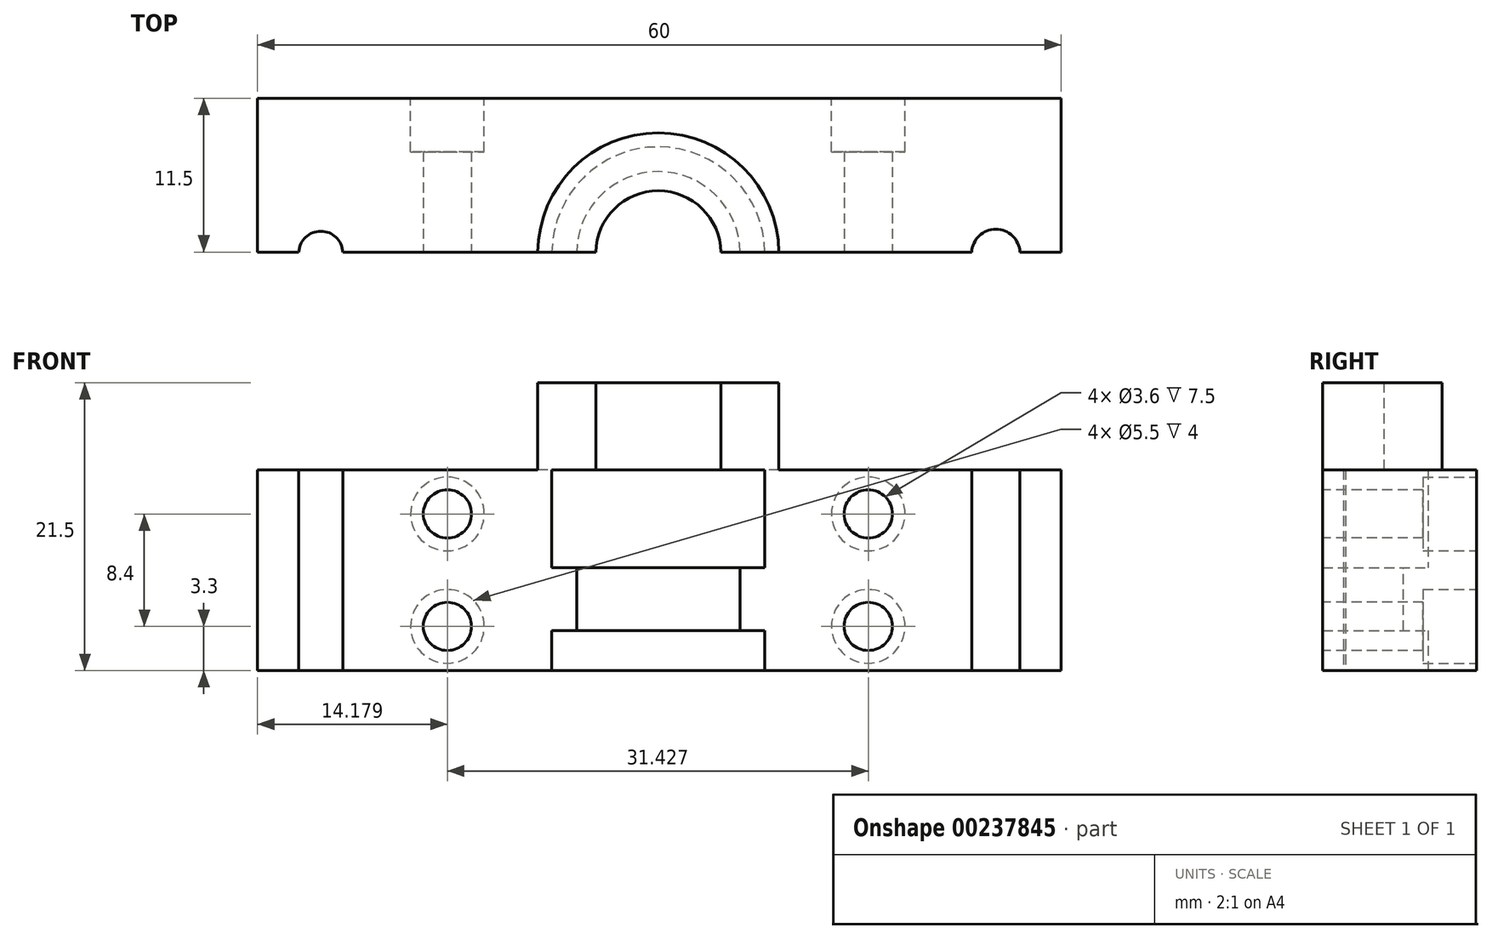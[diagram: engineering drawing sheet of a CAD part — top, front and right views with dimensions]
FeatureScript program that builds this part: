
annotation { "Feature Type Name" : "Feature", "Feature Type Description" : "" }
export const myFeature = defineFeature(function(context is Context, id is Id, definition is map)
    precondition{}
    {
        {
            var Q0;
            Q0=qCreatedBy(makeId("Top.planeOp"),FACE);
            var sketch = newSketch(context, id + "F0", { "sketchPlane" : qUnion([Q0])});
            skArc(sketch, "E0", {"start": v(7.95, 0.09) * mm, "mid": v(0, 7.95) * mm, "end": v(-7.95, 0.09) * mm});
            skArc(sketch, "E1", {"start": v(-23.55, 0.09) * mm, "mid": v(-25.2, 1.65) * mm, "end": v(-26.85, 0.09) * mm});
            skArc(sketch, "E2", {"start": v(27, 0.09) * mm, "mid": v(25.2, 1.8) * mm, "end": v(23.4, 0.09) * mm});
            skLineSegment(sketch, "E3.bottom", {"start": v(-29.93, 11.59) * mm, "end": v(30.07, 11.59) * mm});
            skLineSegment(sketch, "E3.left", {"start": v(-29.93, 11.59) * mm, "end": v(-29.93, 0.09) * mm});
            skLineSegment(sketch, "E3.right", {"start": v(30.07, 11.59) * mm, "end": v(30.07, 0.09) * mm});
            skLineSegment(sketch, "E4", {"start": v(-29.93, 0.09) * mm, "end": v(30.07, 0.09) * mm});
            skSolve(sketch);
        }
        {
            var Q0;
            Q0=makeQuery(id+"F0.imprint","IMPRINT",FACE,{"disambiguationData":[TD([[makeQuery(id+"F0.imprint","IMPRINT",EDGE,{"derivedFrom":sQuery(id+"F0.wireOp",EDGE,"E0")}),-1.0]])]});
            extrude(context, id + "F1", {"entities" : qUnion([Q0]), "depth" : 15 * mm});
        }
        {
            var Q0;
            Q0=qCreatedBy(makeId("Front.planeOp"),FACE);
            var sketch = newSketch(context, id + "F2", { "sketchPlane" : qUnion([Q0])});
            skLineSegment(sketch, "E5.bottom", {"start": v(-8, 7.7) * mm, "end": v(-6.1, 7.7) * mm});
            skLineSegment(sketch, "E5.top", {"start": v(-7.97, 3) * mm, "end": v(-6.1, 3) * mm});
            skLineSegment(sketch, "E5.right", {"start": v(-6.1, 7.7) * mm, "end": v(-6.1, 3) * mm});
            skLineSegment(sketch, "E6", {"start": v(-8, 7.7) * mm, "end": v(-7.97, 3) * mm});
            skLineSegment(sketch, "E7", {"start": v(0, 16.18) * mm, "end": v(0, -1.04) * mm, "construction": true});
            skSolve(sketch);
        }
        {
            var Q0;
            Q0 = qSketchRegion(id + "F2", true);
            var Q1;
            Q1=makeQuery(id+"F1.opExtrude","SWEPT_FACE",FACE,{"disambiguationData":[OSD([sQuery(id+"F0.wireOp",EDGE,"E0")])]});
            revolve(context, id + "F3", {"operationType" : NewBodyOperationType.ADD, "entities" : qUnion([Q0]), "axis" : qUnion([Q1]), "revolveType" : RevolveType.ONE_DIRECTION, "oppositeDirection" : true, "angle" : 180 * degree});
        }
        {
            var Q0;
            {var subQ0=sQuery(id+"F0.wireOp",EDGE,"E4");Q0=makeQuery(id+"F1.opExtrude","SWEPT_FACE",FACE,{"disambiguationData":[OSD([subQ0]),TDD([makeQuery(id+"F0.imprint","IMPRINT",EDGE,{"disambiguationData":[TD([[makeQuery(id+"F0.imprint","INTERSECT",VERTEX,{"disambiguationData":[OD(1.0)],"derivedFrom":[sQuery(id+"F0.wireOp",EDGE,"E0"),subQ0]}),1.0]])],"derivedFrom":subQ0})])]});}
            var sketch = newSketch(context, id + "F4", { "sketchPlane" : qUnion([Q0])});
            skLineSegment(sketch, "E8", {"start": v(-15.75, 15) * mm, "end": v(-15.75, 0) * mm, "construction": true});
            skPoint(sketch, "E9.endSnap0", {"position": v(-23.55, 7.5) * mm});
            skLineSegment(sketch, "E10", {"start": v(-23.55, 7.5) * mm, "end": v(-7.95, 7.5) * mm, "construction": true});
            skCircle(sketch, "E11", {"center": v(-15.75, 11.7) * mm, "radius": 1.8 * mm});
            skCircle(sketch, "E12", {"center": v(-15.75, 3.3) * mm, "radius": 1.8 * mm});
            skSolve(sketch);
        }
        {
            var Q0;
            Q0 = qSketchRegion(id + "F4", true);
            extrude(context, id + "F5", {"entities" : qUnion([Q0]), "operationType" : NewBodyOperationType.REMOVE, "oppositeDirection" : true, "depth" : 25 * mm});
        }
        {
            var Q0;
            {var subQ0=sQuery(id+"F0.wireOp",EDGE,"E4");Q0=makeQuery(id+"F1.opExtrude","SWEPT_FACE",FACE,{"disambiguationData":[OSD([subQ0]),TDD([makeQuery(id+"F0.imprint","IMPRINT",EDGE,{"disambiguationData":[TD([[makeQuery(id+"F0.imprint","INTERSECT",VERTEX,{"disambiguationData":[OD(0.0)],"derivedFrom":[sQuery(id+"F0.wireOp",EDGE,"E0"),subQ0]}),-1.0]])],"derivedFrom":subQ0})])]});}
            var sketch = newSketch(context, id + "F6", { "sketchPlane" : qUnion([Q0])});
            skLineSegment(sketch, "E13", {"start": v(15.68, 15) * mm, "end": v(15.68, 0) * mm, "construction": true});
            skLineSegment(sketch, "E14", {"start": v(23.4, 7.5) * mm, "end": v(7.95, 7.5) * mm, "construction": true});
            skCircle(sketch, "E15", {"center": v(15.68, 11.7) * mm, "radius": 1.8 * mm});
            skCircle(sketch, "E16", {"center": v(15.68, 3.3) * mm, "radius": 1.8 * mm});
            skSolve(sketch);
        }
        {
            var Q0;
            Q0 = qSketchRegion(id + "F6", true);
            extrude(context, id + "F7", {"entities" : qUnion([Q0]), "operationType" : NewBodyOperationType.REMOVE, "oppositeDirection" : true, "depth" : 25 * mm});
        }
        {
            var Q0;
            Q0=makeQuery(id+"F1.opExtrude","CAP_FACE",FACE,{"disambiguationData":[OSD([sQuery(id+"F0.wireOp",EDGE,"E0"),sQuery(id+"F0.wireOp",EDGE,"E1"),sQuery(id+"F0.wireOp",EDGE,"E2"),sQuery(id+"F0.wireOp",EDGE,"E3.bottom"),sQuery(id+"F0.wireOp",EDGE,"E3.left"),sQuery(id+"F0.wireOp",EDGE,"E3.right"),sQuery(id+"F0.wireOp",EDGE,"E4")])],"isStart":false});
            var sketch = newSketch(context, id + "F8", { "sketchPlane" : qUnion([Q0])});
            skArc(sketch, "E17", {"start": v(9, 0.09) * mm, "mid": v(0, 9) * mm, "end": v(-9, 0.09) * mm});
            skLineSegment(sketch, "E18", {"start": v(-9, 0.09) * mm, "end": v(9, 0.09) * mm});
            skSolve(sketch);
        }
        {
            var Q0;
            Q0 = qSketchRegion(id + "F8", true);
            extrude(context, id + "F9", {"entities" : qUnion([Q0]), "operationType" : NewBodyOperationType.ADD, "depth" : 6.5 * mm});
        }
        {
            var Q0;
            Q0=makeQuery(id+"F9.opExtrude","CAP_FACE",FACE,{"disambiguationData":[OSD([sQuery(id+"F8.wireOp",EDGE,"E17"),sQuery(id+"F8.wireOp",EDGE,"E18")])],"isStart":false});
            var sketch = newSketch(context, id + "F10", { "sketchPlane" : qUnion([Q0])});
            skCircle(sketch, "E19", {"center": v(0, 0) * mm, "radius": 4.68 * mm});
            skSolve(sketch);
        }
        {
            var Q0;
            Q0 = qSketchRegion(id + "F10", true);
            extrude(context, id + "F11", {"entities" : qUnion([Q0]), "operationType" : NewBodyOperationType.REMOVE, "oppositeDirection" : true, "depth" : 25 * mm});
        }
        {
            var Q0;
            Q0=makeQuery(id+"F1.opExtrude","CAP_FACE",FACE,{"disambiguationData":[OSD([sQuery(id+"F0.wireOp",EDGE,"E0"),sQuery(id+"F0.wireOp",EDGE,"E1"),sQuery(id+"F0.wireOp",EDGE,"E2"),sQuery(id+"F0.wireOp",EDGE,"E3.bottom"),sQuery(id+"F0.wireOp",EDGE,"E3.left"),sQuery(id+"F0.wireOp",EDGE,"E3.right"),sQuery(id+"F0.wireOp",EDGE,"E4")])],"isStart":true});
            var sketch = newSketch(context, id + "F12", { "sketchPlane" : qUnion([Q0])});
            skLineSegment(sketch, "E20.bottom", {"start": v(30.07, -0.09) * mm, "end": v(-30.35, -0.09) * mm});
            skLineSegment(sketch, "E20.top", {"start": v(30.07, 4.05) * mm, "end": v(-30.35, 4.05) * mm});
            skLineSegment(sketch, "E20.left", {"start": v(30.07, -0.09) * mm, "end": v(30.07, 4.05) * mm});
            skLineSegment(sketch, "E20.right", {"start": v(-30.35, -0.09) * mm, "end": v(-30.35, 4.05) * mm});
            skSolve(sketch);
        }
        {
            var Q0;
            Q0 = qSketchRegion(id + "F12", true);
            extrude(context, id + "F13", {"entities" : qUnion([Q0]), "operationType" : NewBodyOperationType.REMOVE, "endBound" : BoundingType.THROUGH_ALL, "oppositeDirection" : true, "depth" : 25 * mm});
        }
        {
            var Q0;
            Q0=makeQuery(id+"F1.opExtrude","SWEPT_FACE",FACE,{"disambiguationData":[OSD([sQuery(id+"F0.wireOp",EDGE,"E3.bottom")])]});
            var sketch = newSketch(context, id + "F14", { "sketchPlane" : qUnion([Q0])});
            skCircle(sketch, "E21", {"center": v(-15.68, 11.7) * mm, "radius": 2.75 * mm});
            skCircle(sketch, "E22", {"center": v(-15.68, 3.3) * mm, "radius": 2.75 * mm});
            skCircle(sketch, "E23", {"center": v(15.75, 11.7) * mm, "radius": 2.75 * mm});
            skCircle(sketch, "E24", {"center": v(15.75, 3.3) * mm, "radius": 2.75 * mm});
            skSolve(sketch);
        }
        {
            var Q0;
            Q0=makeQuery(id+"F14.imprint","IMPRINT",FACE,{"disambiguationData":[TD([[makeQuery(id+"F14.imprint","IMPRINT",EDGE,{"derivedFrom":sQuery(id+"F14.wireOp",EDGE,"E21")}),1.0]])]});
            var Q1;
            Q1=makeQuery(id+"F14.imprint","IMPRINT",FACE,{"disambiguationData":[TD([[makeQuery(id+"F14.imprint","IMPRINT",EDGE,{"derivedFrom":sQuery(id+"F14.wireOp",EDGE,"E23")}),1.0]])]});
            var Q2;
            Q2=makeQuery(id+"F14.imprint","IMPRINT",FACE,{"disambiguationData":[TD([[makeQuery(id+"F14.imprint","IMPRINT",EDGE,{"derivedFrom":sQuery(id+"F14.wireOp",EDGE,"E22")}),1.0]])]});
            var Q3;
            Q3=makeQuery(id+"F14.imprint","IMPRINT",FACE,{"disambiguationData":[TD([[makeQuery(id+"F14.imprint","IMPRINT",EDGE,{"derivedFrom":sQuery(id+"F14.wireOp",EDGE,"E24")}),1.0]])]});
            var Q4;
            Q4=sQuery(id+"F14.wireOp",EDGE,"E21");
            extrude(context, id + "F15", {"entities" : qUnion([Q0, Q1, Q2, Q3]), "operationType" : NewBodyOperationType.REMOVE, "surfaceEntities" : qUnion([Q4]), "oppositeDirection" : true, "depth" : 4 * mm});
        }
    });
